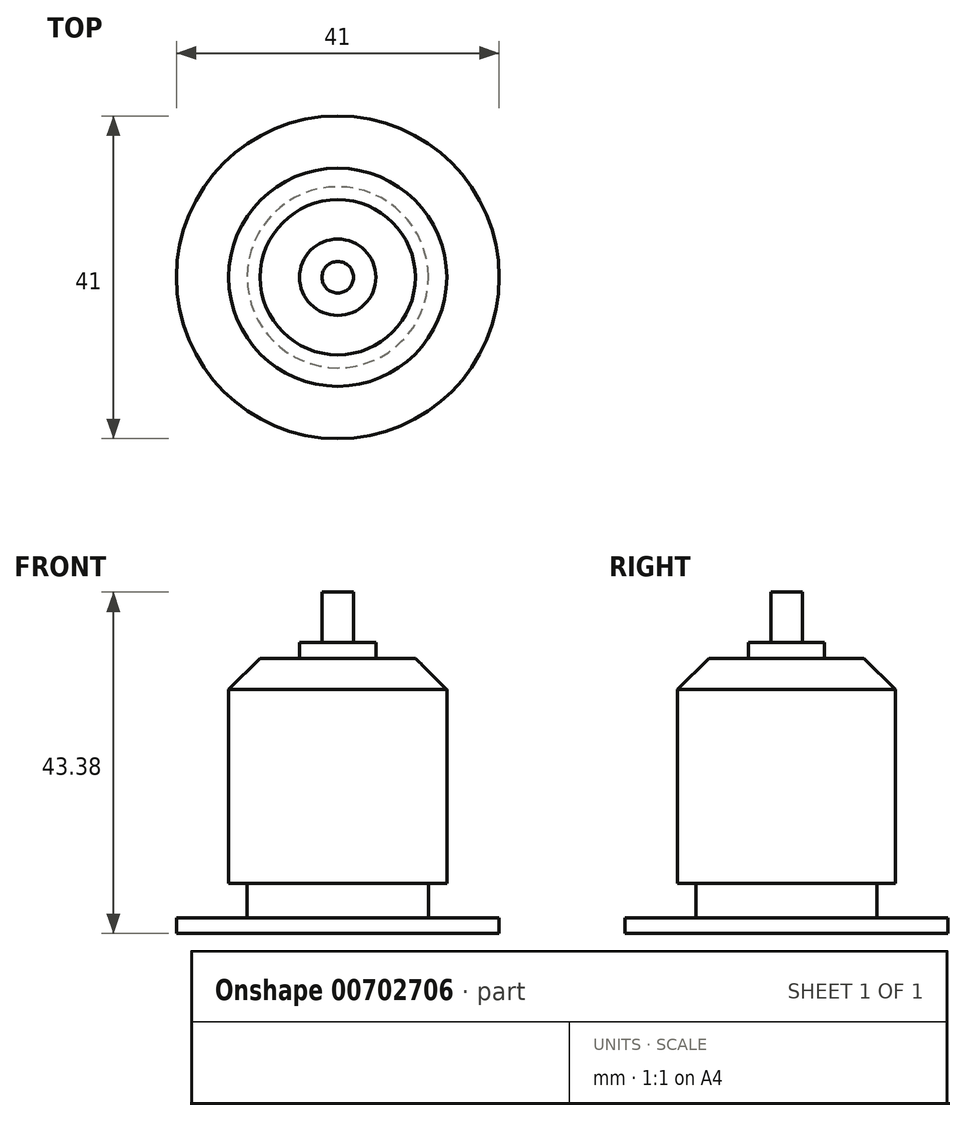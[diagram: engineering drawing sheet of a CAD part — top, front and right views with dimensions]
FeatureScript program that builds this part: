
annotation { "Feature Type Name" : "Feature", "Feature Type Description" : "" }
export const myFeature = defineFeature(function(context is Context, id is Id, definition is map)
    precondition{}
    {
        {
            var Q0;
            Q0=qCreatedBy(makeId("Front.planeOp"),FACE);
            var sketch = newSketch(context, id + "F0", { "sketchPlane" : qUnion([Q0])});
            skLineSegment(sketch, "E0", {"start": v(0, 0) * mm, "end": v(0, 43.38) * mm, "construction": true});
            skLineSegment(sketch, "E1", {"start": v(0, 0) * mm, "end": v(20.5, 0) * mm});
            skLineSegment(sketch, "E2", {"start": v(20.5, 0) * mm, "end": v(20.5, 2) * mm});
            skLineSegment(sketch, "E3", {"start": v(20.5, 2) * mm, "end": v(11.5, 2) * mm});
            skLineSegment(sketch, "E4", {"start": v(11.5, 2) * mm, "end": v(11.5, 6.38) * mm});
            skLineSegment(sketch, "E5", {"start": v(11.5, 6.38) * mm, "end": v(13.85, 6.38) * mm});
            skLineSegment(sketch, "E6", {"start": v(13.85, 6.38) * mm, "end": v(13.85, 30.99) * mm});
            skLineSegment(sketch, "E7", {"start": v(13.85, 30.99) * mm, "end": v(9.85, 34.99) * mm});
            skLineSegment(sketch, "E8", {"start": v(9.85, 34.99) * mm, "end": v(4.85, 34.99) * mm});
            skLineSegment(sketch, "E9", {"start": v(4.85, 34.99) * mm, "end": v(4.85, 37) * mm});
            skLineSegment(sketch, "E10", {"start": v(4.85, 37) * mm, "end": v(2, 37) * mm});
            skLineSegment(sketch, "E11", {"start": v(2, 37) * mm, "end": v(2, 43.38) * mm});
            skLineSegment(sketch, "E12", {"start": v(2, 43.38) * mm, "end": v(0, 43.38) * mm});
            skLineSegment(sketch, "E13", {"start": v(0, 43.38) * mm, "end": v(0, 0) * mm});
            skSolve(sketch);
        }
        {
            var Q0;
            Q0=makeQuery(id+"F0.imprint","IMPRINT",FACE,{"disambiguationData":[TD([[makeQuery(id+"F0.imprint","IMPRINT",EDGE,{"derivedFrom":sQuery(id+"F0.wireOp",EDGE,"E1")}),1.0]])]});
            var Q1;
            Q1=sQuery(id+"F0.wireOp",EDGE,"E13");
            revolve(context, id + "F1", {"surfaceOperationType" : NewSurfaceOperationType.NEW, "entities" : qUnion([Q0]), "axis" : qUnion([Q1]), "revolveType" : RevolveType.FULL});
        }
    });
